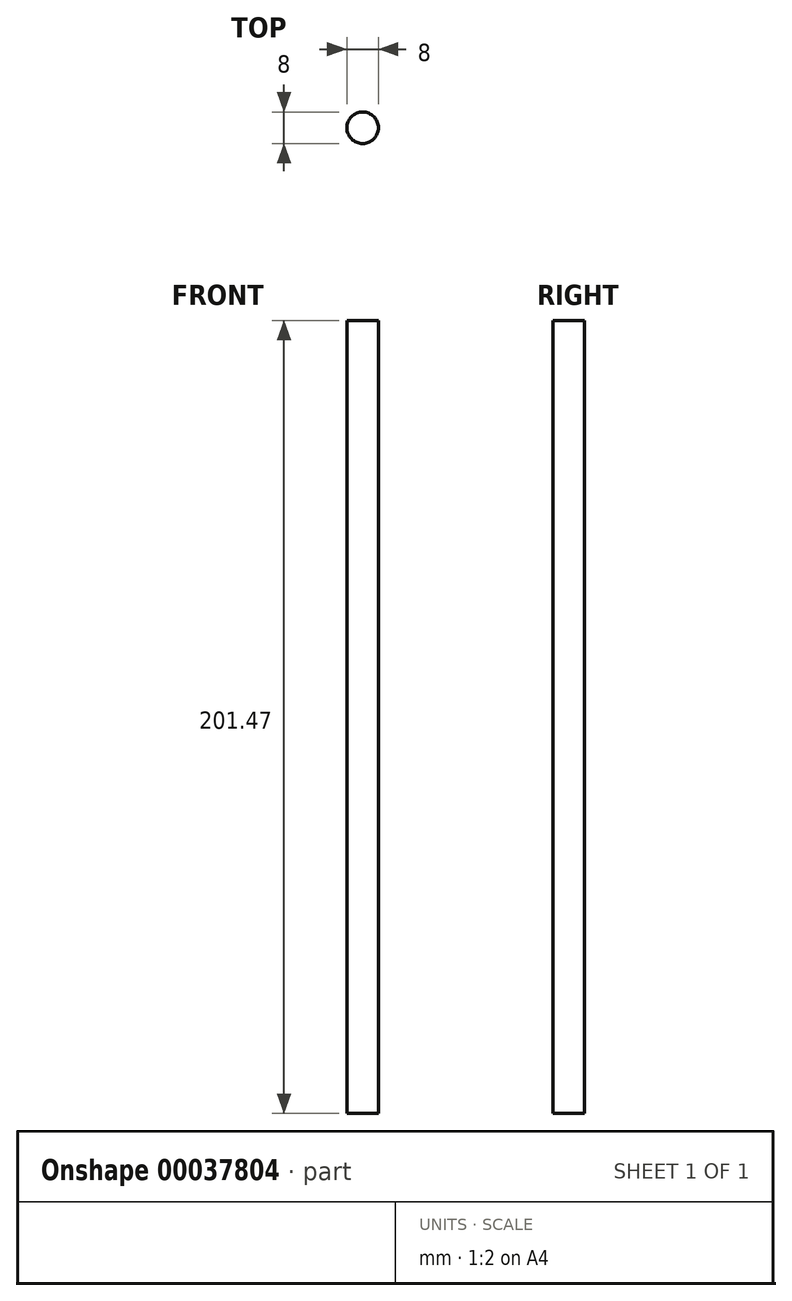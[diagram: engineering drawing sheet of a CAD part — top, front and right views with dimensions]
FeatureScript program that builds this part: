
annotation { "Feature Type Name" : "Feature", "Feature Type Description" : "" }
export const myFeature = defineFeature(function(context is Context, id is Id, definition is map)
    precondition{}
    {
        {
            var Q0;
            Q0=qCreatedBy(makeId("Top.planeOp"),FACE);
            var sketch = newSketch(context, id + "F0", { "sketchPlane" : qUnion([Q0])});
            skCircle(sketch, "E0", {"center": v(0, 0) * mm, "radius": 4 * mm});
            skSolve(sketch);
        }
        {
            var Q0;
            Q0=qSketchRegion(id+"F0",true);
            extrude(context, id + "F1", {"entities" : qUnion([Q0]), "depth" : 201.47 * mm});
        }
    });
